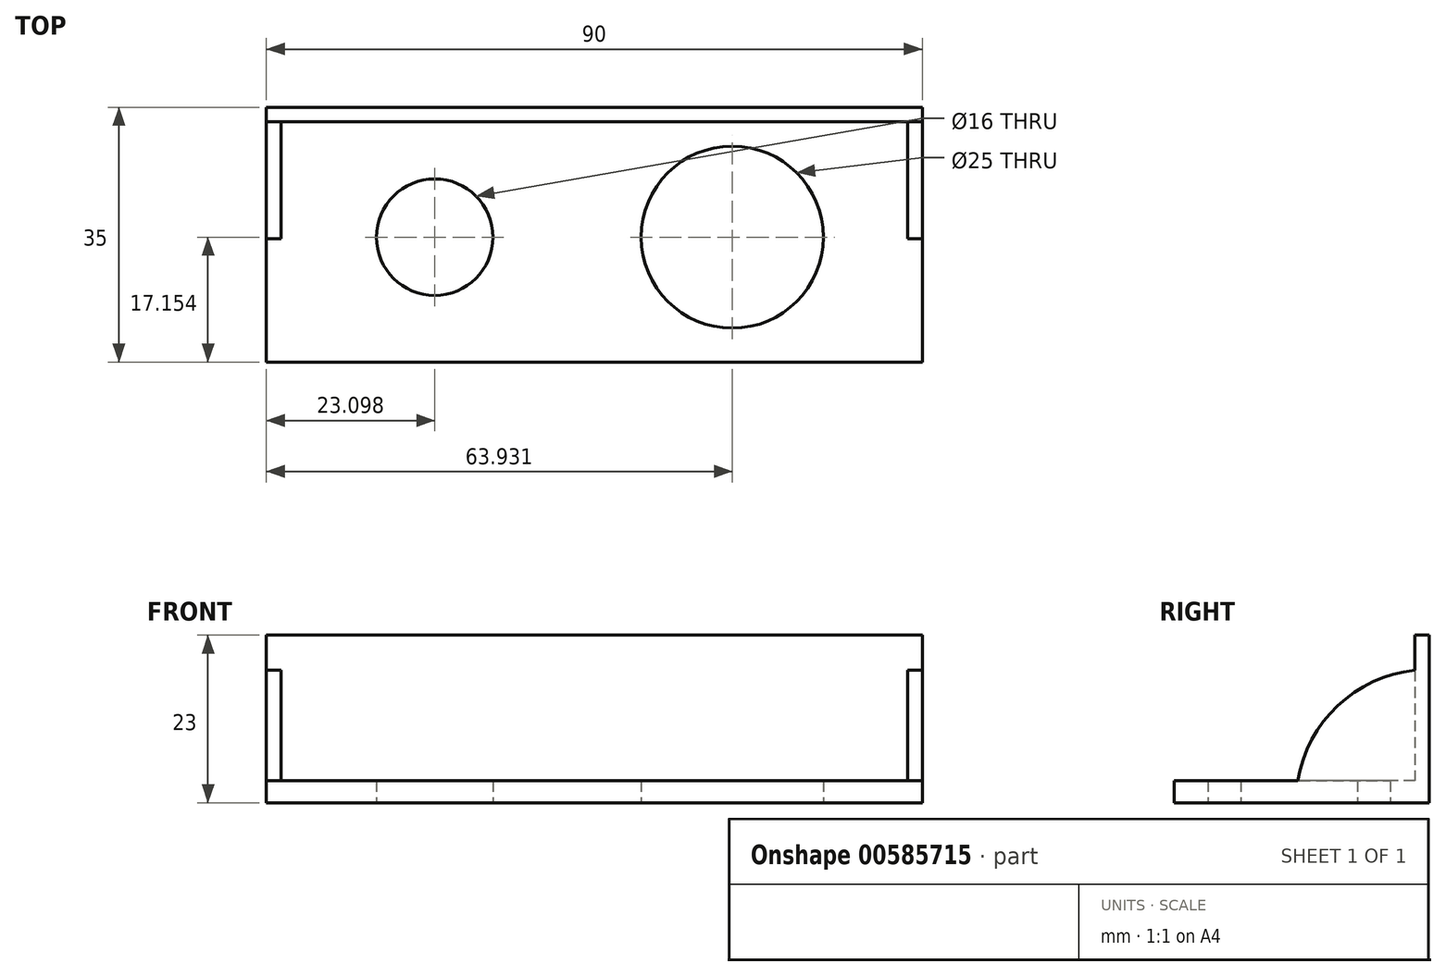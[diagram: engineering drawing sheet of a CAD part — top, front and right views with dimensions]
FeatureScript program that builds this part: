
annotation { "Feature Type Name" : "Feature", "Feature Type Description" : "" }
export const myFeature = defineFeature(function(context is Context, id is Id, definition is map)
    precondition{}
    {
        {
            var Q0;
            Q0=qCreatedBy(makeId("Top.planeOp"),FACE);
            var sketch = newSketch(context, id + "F0", { "sketchPlane" : qUnion([Q0])});
            skLineSegment(sketch, "E0.bottom", {"start": v(-45, 0) * mm, "end": v(45, 0) * mm});
            skLineSegment(sketch, "E0.top", {"start": v(-45, -35) * mm, "end": v(45, -35) * mm});
            skLineSegment(sketch, "E0.left", {"start": v(-45, 0) * mm, "end": v(-45, -35) * mm});
            skLineSegment(sketch, "E0.right", {"start": v(45, 0) * mm, "end": v(45, -35) * mm});
            skSolve(sketch);
        }
        {
            var Q0;
            Q0 = qSketchRegion(id + "F0", true);
            extrude(context, id + "F1", {"entities" : qUnion([Q0]), "depth" : 3 * mm, "offsetDistance" : 25 * mm});
        }
        {
            var Q0;
            Q0=qCreatedBy(makeId("Front.planeOp"),FACE);
            var sketch = newSketch(context, id + "F2", { "sketchPlane" : qUnion([Q0])});
            skLineSegment(sketch, "E1.bottom", {"start": v(-45, 0) * mm, "end": v(45, 0) * mm});
            skLineSegment(sketch, "E1.top", {"start": v(-45, 23) * mm, "end": v(45, 23) * mm});
            skLineSegment(sketch, "E1.left", {"start": v(-45, 0) * mm, "end": v(-45, 23) * mm});
            skLineSegment(sketch, "E1.right", {"start": v(45, 0) * mm, "end": v(45, 23) * mm});
            skSolve(sketch);
        }
        {
            var Q0;
            Q0 = qSketchRegion(id + "F2", true);
            extrude(context, id + "F3", {"entities" : qUnion([Q0]), "operationType" : NewBodyOperationType.ADD, "depth" : 2 * mm, "offsetDistance" : 25 * mm});
        }
        {
            var Q0;
            Q0=qCreatedBy(makeId("Right.planeOp"),FACE);
            var sketch = newSketch(context, id + "F4", { "sketchPlane" : qUnion([Q0])});
            skLineSegment(sketch, "E2.bottom", {"start": v(0, 0) * mm, "end": v(-18.3, 0) * mm});
            skLineSegment(sketch, "E2.top", {"start": v(0, 18.3) * mm, "end": v(0, 18.3) * mm});
            skLineSegment(sketch, "E2.left", {"start": v(0, 0) * mm, "end": v(0, 18.3) * mm});
            skLineSegment(sketch, "E2.right", {"start": v(-18.3, 0) * mm, "end": v(-18.3, 0) * mm});
            skPoint(sketch, "E3.visualSharp", {"position": v(-18.3, 18.3) * mm});
            skArc(sketch, "E3.filletArc", {"start": v(0, 18.3) * mm, "mid": v(-12.95, 12.95) * mm, "end": v(-18.3, 0) * mm});
            skSolve(sketch);
        }
        {
            var Q0;
            Q0 = qSketchRegion(id + "F4", true);
            extrude(context, id + "F5", {"entities" : qUnion([Q0]), "operationType" : NewBodyOperationType.ADD, "depth" : 45 * mm, "offsetDistance" : 25 * mm, "hasSecondDirection" : true, "secondDirectionOppositeDirection" : true, "secondDirectionDepth" : 45 * mm});
        }
        {
            var Q0;
            Q0=qCreatedBy(makeId("Top.planeOp"),FACE);
            var sketch = newSketch(context, id + "F6", { "sketchPlane" : qUnion([Q0])});
            skLineSegment(sketch, "E4.bottom", {"start": v(-43, -2) * mm, "end": v(43, -2) * mm});
            skLineSegment(sketch, "E4.top", {"start": v(-43, -35) * mm, "end": v(43, -35) * mm});
            skLineSegment(sketch, "E4.left", {"start": v(-43, -2) * mm, "end": v(-43, -35) * mm});
            skLineSegment(sketch, "E4.right", {"start": v(43, -2) * mm, "end": v(43, -35) * mm});
            skSolve(sketch);
        }
        {
            var Q0;
            Q0 = qSketchRegion(id + "F6", true);
            extrude(context, id + "F7", {"entities" : qUnion([Q0]), "operationType" : NewBodyOperationType.REMOVE, "depth" : 35.9 * mm, "offsetDistance" : 25 * mm, "hasSecondDirection" : true, "secondDirectionOppositeDirection" : false, "secondDirectionDepth" : 3 * mm});
        }
        {
            var Q0;
            Q0=qCreatedBy(makeId("Top.planeOp"),FACE);
            var sketch = newSketch(context, id + "F8", { "sketchPlane" : qUnion([Q0])});
            skCircle(sketch, "E5", {"center": v(18.93, -17.85) * mm, "radius": 12.5 * mm});
            skCircle(sketch, "E6", {"center": v(-21.9, -17.85) * mm, "radius": 8 * mm});
            skSolve(sketch);
        }
        {
            var Q0;
            Q0 = qSketchRegion(id + "F8", true);
            extrude(context, id + "F9", {"entities" : qUnion([Q0]), "operationType" : NewBodyOperationType.REMOVE, "depth" : 3 * mm, "offsetDistance" : 25 * mm});
        }
    });
